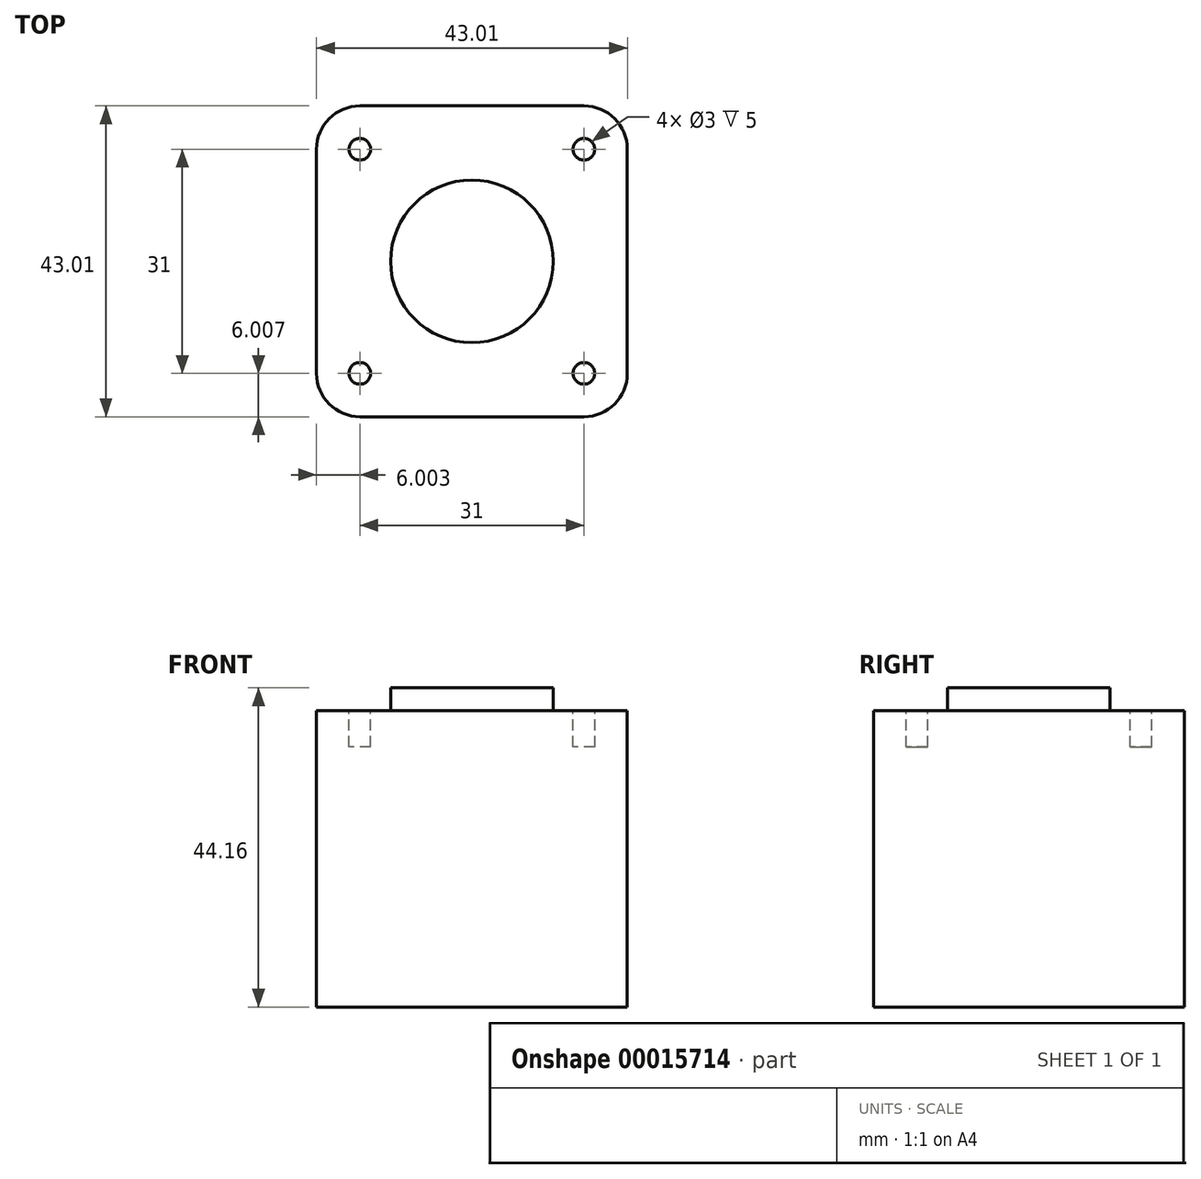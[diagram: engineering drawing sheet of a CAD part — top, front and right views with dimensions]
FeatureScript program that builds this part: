
annotation { "Feature Type Name" : "Feature", "Feature Type Description" : "" }
export const myFeature = defineFeature(function(context is Context, id is Id, definition is map)
    precondition{}
    {
        {
            var Q0;
            Q0=qCreatedBy(makeId("Top.planeOp"),FACE);
            var sketch = newSketch(context, id + "F0", { "sketchPlane" : qUnion([Q0])});
            skLineSegment(sketch, "E0.bottom", {"start": v(0, 0) * mm, "end": v(43, 0) * mm});
            skLineSegment(sketch, "E0.top", {"start": v(0, -43) * mm, "end": v(43, -43) * mm});
            skLineSegment(sketch, "E0.left", {"start": v(0, 0) * mm, "end": v(0, -43) * mm});
            skLineSegment(sketch, "E0.right", {"start": v(43, 0) * mm, "end": v(43, -43) * mm});
            skSolve(sketch);
        }
        {
            var Q0;
            Q0=makeQuery(id+"F0.imprint","IMPRINT",FACE,{"disambiguationData":[TD([[makeQuery(id+"F0.imprint","IMPRINT",EDGE,{"derivedFrom":sQuery(id+"F0.wireOp",EDGE,"E0.bottom")}),-1.0]])]});
            extrude(context, id + "F1", {"entities" : qUnion([Q0]), "depth" : 40.98 * mm});
        }
        {
            var Q0;
            Q0=makeQuery(id+"F1.opExtrude","SWEPT_EDGE",EDGE,{"disambiguationData":[OSD([sQuery(id+"F0.wireOp",EDGE,"E0.top"),sQuery(id+"F0.wireOp",EDGE,"E0.left")])]});
            var Q1;
            Q1=makeQuery(id+"F1.opExtrude","SWEPT_EDGE",EDGE,{"disambiguationData":[OSD([sQuery(id+"F0.wireOp",EDGE,"E0.top"),sQuery(id+"F0.wireOp",EDGE,"E0.right")])]});
            var Q2;
            Q2=makeQuery(id+"F1.opExtrude","SWEPT_EDGE",EDGE,{"disambiguationData":[OSD([sQuery(id+"F0.wireOp",EDGE,"E0.bottom"),sQuery(id+"F0.wireOp",EDGE,"E0.right")])]});
            var Q3;
            Q3=makeQuery(id+"F1.opExtrude","SWEPT_EDGE",EDGE,{"disambiguationData":[OSD([sQuery(id+"F0.wireOp",EDGE,"E0.bottom"),sQuery(id+"F0.wireOp",EDGE,"E0.left")])]});
            fillet(context, id + "F2", {"entities" : qUnion([Q0, Q1, Q2, Q3]), "radius" : 6 * mm, "tangentPropagation" : true, "allowEdgeOverflow" : false});
        }
        {
            var Q0;
            Q0=makeQuery(id+"F1.opExtrude","CAP_FACE",FACE,{"disambiguationData":[OSD([sQuery(id+"F0.wireOp",EDGE,"E0.bottom"),sQuery(id+"F0.wireOp",EDGE,"E0.top"),sQuery(id+"F0.wireOp",EDGE,"E0.left"),sQuery(id+"F0.wireOp",EDGE,"E0.right")])],"isStart":false});
            var sketch = newSketch(context, id + "F3", { "sketchPlane" : qUnion([Q0])});
            skLineSegment(sketch, "E1", {"start": v(37, -6) * mm, "end": v(37, -37) * mm});
            skLineSegment(sketch, "E2", {"start": v(6, -6) * mm, "end": v(6, -37) * mm});
            skLineSegment(sketch, "E3", {"start": v(6, -21.5) * mm, "end": v(37, -21.5) * mm});
            skPoint(sketch, "E4", {"position": v(21.5, -21.5) * mm});
            skCircle(sketch, "E5", {"center": v(6, -37) * mm, "radius": 1.5 * mm});
            skCircle(sketch, "E6", {"center": v(37, -37) * mm, "radius": 1.5 * mm});
            skCircle(sketch, "E7", {"center": v(37, -6) * mm, "radius": 1.5 * mm});
            skCircle(sketch, "E8", {"center": v(6, -6) * mm, "radius": 1.5 * mm});
            skLineSegment(sketch, "E9", {"start": v(21.5, 0) * mm, "end": v(21.5, -43) * mm});
            skSolve(sketch);
        }
        {
            var Q0;
            Q0=qSketchRegion(id+"F3",true);
            extrude(context, id + "F4", {"entities" : qUnion([Q0]), "operationType" : NewBodyOperationType.REMOVE, "oppositeDirection" : true, "depth" : 5 * mm});
        }
        {
            var Q0;
            Q0=makeQuery(id+"F1.opExtrude","CAP_FACE",FACE,{"disambiguationData":[OSD([sQuery(id+"F0.wireOp",EDGE,"E0.bottom"),sQuery(id+"F0.wireOp",EDGE,"E0.top"),sQuery(id+"F0.wireOp",EDGE,"E0.left"),sQuery(id+"F0.wireOp",EDGE,"E0.right")])],"isStart":false});
            var sketch = newSketch(context, id + "F5", { "sketchPlane" : qUnion([Q0])});
            skCircle(sketch, "E10", {"center": v(21.5, -21.5) * mm, "radius": 11.25 * mm});
            skLineSegment(sketch, "E11", {"start": v(21.5, 0) * mm, "end": v(21.5, -43) * mm});
            skSolve(sketch);
        }
        {
            var Q0;
            {var subQ0=makeQuery(id+"F5.imprint","IMPRINT",EDGE,{"derivedFrom":makeQuery(id+"FrR7yDf3rcl6F0C_1.opExtrude","CAP_EDGE",EDGE,{"disambiguationData":[OSD([sQuery(id+"F5JGNH1QvfmkxMA_1.wireOp",EDGE,"f4951451-9bfc-4b5e-bbcf-62f7722cc768")])],"isStart":true})});Q0=qUnion([makeQuery(id+"F5.imprint","IMPRINT",FACE,{"disambiguationData":[TD([[subQ0,1.0]])]}),makeQuery(id+"F5.imprint","IMPRINT",FACE,{"disambiguationData":[TD([[makeQuery(id+"F5.imprint","IMPRINT",EDGE,{"derivedFrom":sQuery(id+"F5.wireOp",EDGE,"E10")}),1.0]])]})]);}
            extrude(context, id + "F6", {"entities" : qUnion([Q0]), "operationType" : NewBodyOperationType.ADD, "depth" : 3.17 * mm});
        }
    });
